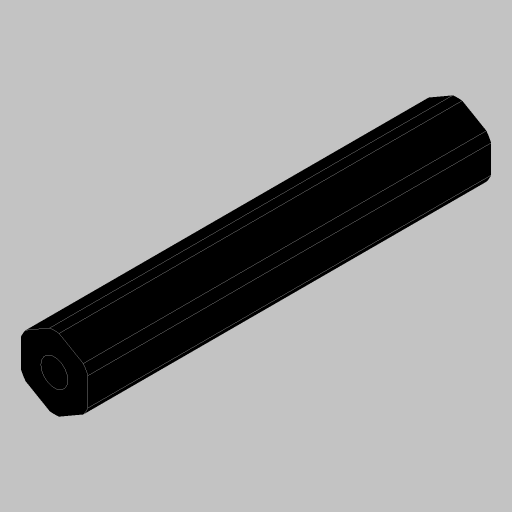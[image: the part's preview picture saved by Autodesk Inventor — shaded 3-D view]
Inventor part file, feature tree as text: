
AUTODESK INVENTOR PART (.ipt)
format: ipt  version: 2023.5 (Build 275446000, 446)  size: 193,536 bytes
history: native  units: in
note: dims shown in document units (in); Inventor stores cm internally (conversion verified against a paired STEP export)
features: extrude x2, projected_geometry x2, hole x1
ambient origin geometry x8: Origin, YZ Plane, XZ Plane, XY Plane, X Axis, Y Axis, Z Axis, Center Point
bodies: Solid1 (feature_tree)
feature tree (5):
  extrude  "Extrusion1"  TaperAngle=0.0deg  [1 undecoded]
  hole  "Hole1"  [1 undecoded]
  extrude  "Extrusion3"  TaperAngle=0.0deg  [1 undecoded]
  projected_geometry  "Project Cut Edges1"
  projected_geometry  "Project Cut Edges2"
note: 3 required parameter values undecoded (feature->parameter linkage not recoverable at this tier; creation-order binding heuristic only, values carry confidence <= 0.55)
